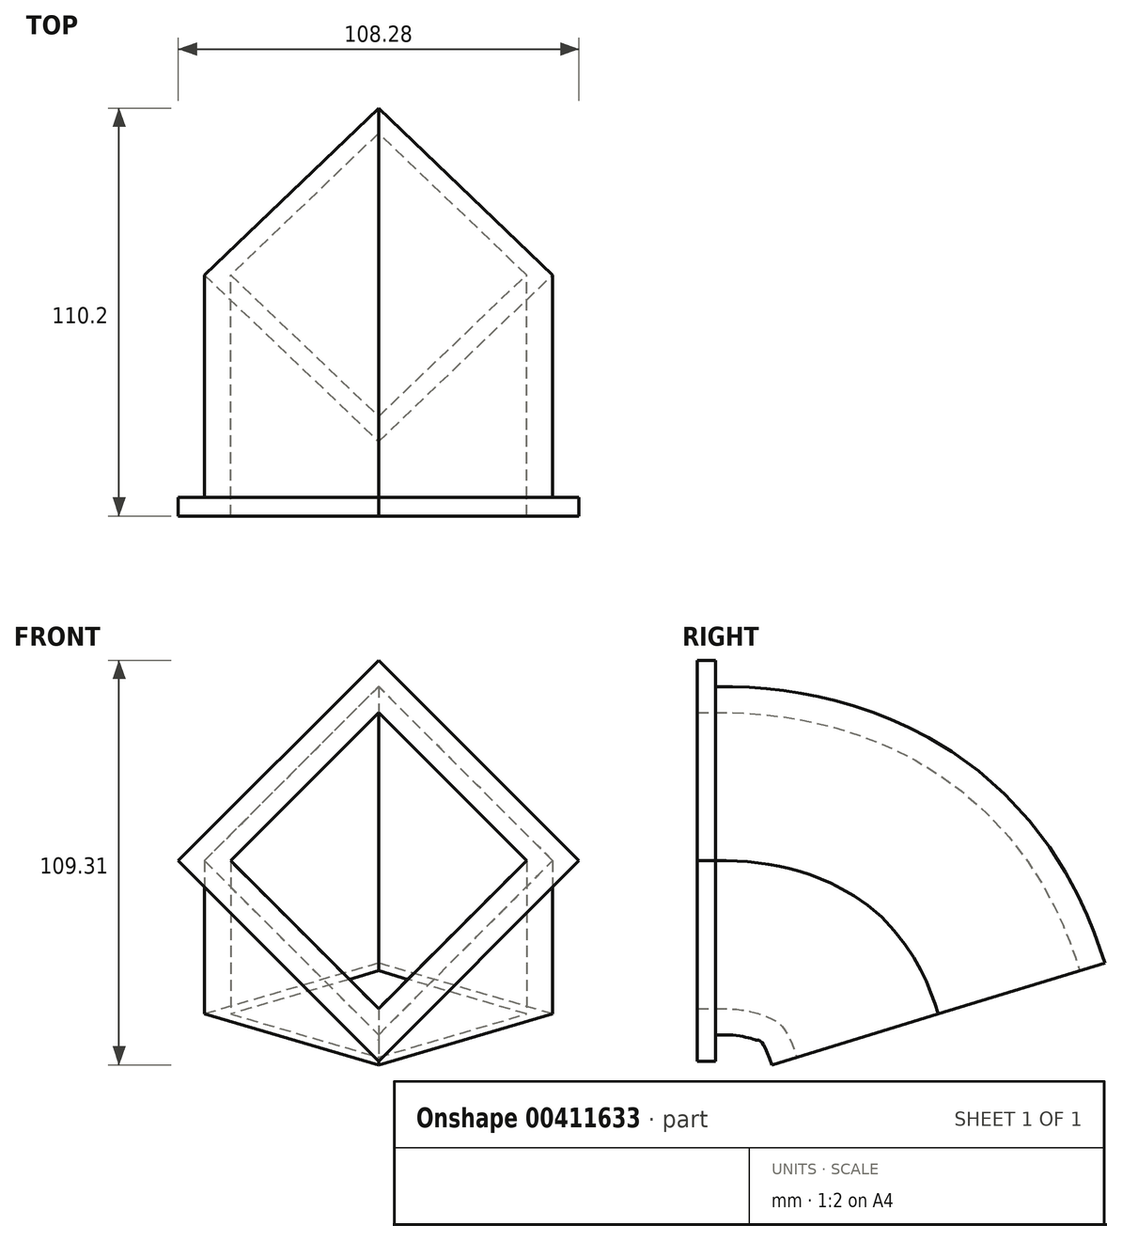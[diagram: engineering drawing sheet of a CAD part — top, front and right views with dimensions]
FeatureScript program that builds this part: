
annotation { "Feature Type Name" : "Feature", "Feature Type Description" : "" }
export const myFeature = defineFeature(function(context is Context, id is Id, definition is map)
    precondition{}
    {
        {
            var Q0;
            Q0=qCreatedBy(makeId("Front.planeOp"),FACE);
            var sketch = newSketch(context, id + "F0", { "sketchPlane" : qUnion([Q0])});
            skLineSegment(sketch, "E0", {"start": v(0, 0) * mm, "end": v(40, 40) * mm});
            skLineSegment(sketch, "E1", {"start": v(40, 40) * mm, "end": v(0, 80) * mm});
            skLineSegment(sketch, "E2", {"start": v(0, 80) * mm, "end": v(-40, 40) * mm});
            skLineSegment(sketch, "E3", {"start": v(-40, 40) * mm, "end": v(0, 0) * mm});
            skLineSegment(sketch, "E4.0", {"start": v(0, -7.07) * mm, "end": v(47.07, 40) * mm});
            skLineSegment(sketch, "E4.1", {"start": v(-47.07, 40) * mm, "end": v(0, -7.07) * mm});
            skLineSegment(sketch, "E4.2", {"start": v(0, 87.07) * mm, "end": v(-47.07, 40) * mm});
            skLineSegment(sketch, "E4.3", {"start": v(47.07, 40) * mm, "end": v(0, 87.07) * mm});
            skSolve(sketch);
        }
        {
            var Q0;
            Q0=qCreatedBy(makeId("Right.planeOp"),FACE);
            var sketch = newSketch(context, id + "F1", { "sketchPlane" : qUnion([Q0])});
            skFitSpline(sketch, "E5", {"points": [v(1.65, 0) * mm, v(15.1, -2.8) * mm, v(22.4, -14.69) * mm], "startDerivative": vector(35.23, 0) * mm, "endDerivative": vector(14.7, -48.08) * mm});
            skSolve(sketch);
        }
        {
            var Q0;
            Q0=makeQuery(id+"F0.imprint","IMPRINT",FACE,{"disambiguationData":[TD([[makeQuery(id+"F0.imprint","IMPRINT",EDGE,{"derivedFrom":sQuery(id+"F0.wireOp",EDGE,"E0")}),-1.0]])]});
            var Q1;
            Q1=sQuery(id+"F1.wireOp",EDGE,"E5");
            sweep(context, id + "F2", {"profiles" : qUnion([Q0]), "path" : qUnion([Q1])});
        }
        {
            var Q0;
            Q0=makeQuery(id+"F2.opSweep","CAP_FACE",FACE,{"disambiguationData":[OSD([sQuery(id+"F0.wireOp",EDGE,"E0"),sQuery(id+"F0.wireOp",EDGE,"E1"),sQuery(id+"F0.wireOp",EDGE,"E2"),sQuery(id+"F0.wireOp",EDGE,"E3"),sQuery(id+"F0.wireOp",EDGE,"E4.0"),sQuery(id+"F0.wireOp",EDGE,"E4.1"),sQuery(id+"F0.wireOp",EDGE,"E4.2"),sQuery(id+"F0.wireOp",EDGE,"E4.3"),sQuery(id+"F1.wireOp",VERTEX,"E5.start")])],"isStart":true});
            extrude(context, id + "F3", {"entities" : qUnion([Q0]), "operationType" : NewBodyOperationType.ADD, "depth" : 5 * mm});
        }
        {
            var Q0;
            Q0=qCreatedBy(makeId("Front.planeOp"),FACE);
            var sketch = newSketch(context, id + "F4", { "sketchPlane" : qUnion([Q0])});
            skLineSegment(sketch, "E6.0", {"start": v(0, 94.14) * mm, "end": v(54.14, 40) * mm});
            skLineSegment(sketch, "E6.1", {"start": v(-54.14, 40) * mm, "end": v(0, 94.14) * mm});
            skLineSegment(sketch, "E6.2", {"start": v(0, -14.14) * mm, "end": v(-54.14, 40) * mm});
            skLineSegment(sketch, "E6.3", {"start": v(54.14, 40) * mm, "end": v(0, -14.14) * mm});
            skLineSegment(sketch, "E7.0", {"start": v(0, 80) * mm, "end": v(-40, 40) * mm});
            skLineSegment(sketch, "E7.1", {"start": v(40, 40) * mm, "end": v(0, 80) * mm});
            skLineSegment(sketch, "E7.2", {"start": v(0, 0) * mm, "end": v(40, 40) * mm});
            skLineSegment(sketch, "E7.3", {"start": v(-40, 40) * mm, "end": v(0, 0) * mm});
            skSolve(sketch);
        }
        {
            var Q0;
            Q0 = qSketchRegion(id + "F4", true);
            extrude(context, id + "F5", {"entities" : qUnion([Q0]), "operationType" : NewBodyOperationType.ADD, "depth" : 5 * mm});
        }
    });
